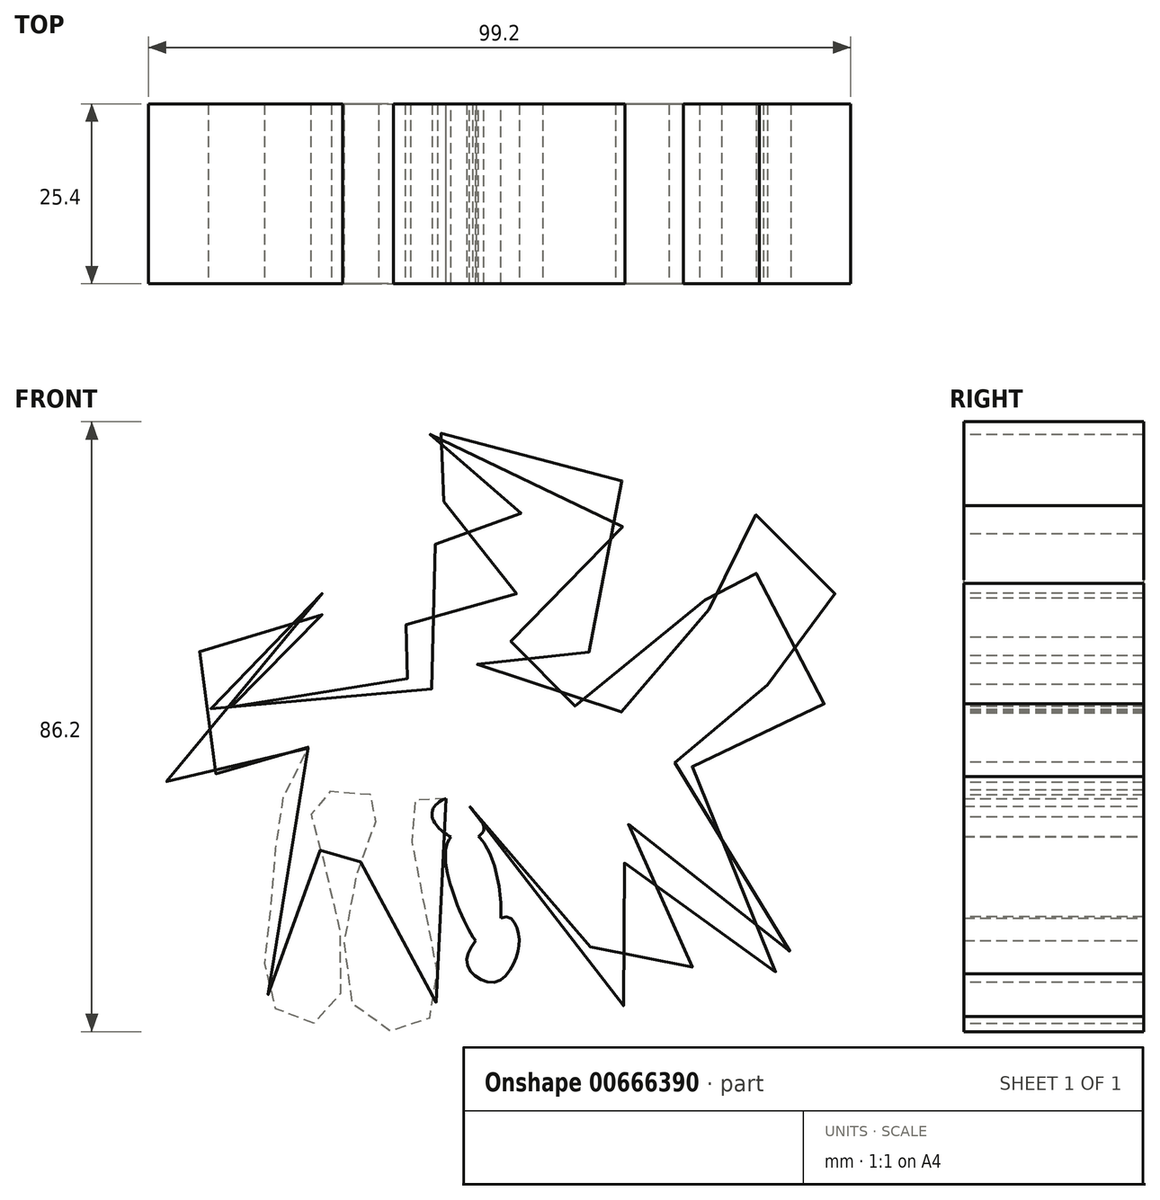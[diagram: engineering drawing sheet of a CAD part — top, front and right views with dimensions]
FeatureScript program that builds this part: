
annotation { "Feature Type Name" : "Feature", "Feature Type Description" : "" }
export const myFeature = defineFeature(function(context is Context, id is Id, definition is map)
    precondition{}
    {
        {
            var Q0;
            Q0=qCreatedBy(makeId("Front.planeOp"),FACE);
            var sketch = newSketch(context, id + "F0", { "sketchPlane" : qUnion([Q0])});
            skFitSpline(sketch, "E0", {"points": [v(-24.68, 12.83) * mm, v(-33.88, 23.4) * mm, v(-26.05, 37.12) * mm, v(-17.24, 28.1) * mm, v(-16.26, 38.88) * mm, v(-34.86, 43.38) * mm, v(-34.47, 50.63) * mm, v(-31.53, 51.22) * mm, v(-7.05, 52) * mm, v(-3.53, 39.27) * mm, v(-4.7, 23.01) * mm, v(-14.1, 20.27) * mm, v(-22.52, 22.43) * mm, v(-24.1, 18.9) * mm, v(-19.78, 15.38) * mm, v(-7.44, 12.44) * mm, v(8.81, 14.2) * mm, v(8.62, 26.74) * mm, v(5.68, 37.7) * mm, v(15.08, 40.25) * mm, v(15.86, 29.09) * mm, v(25.46, 29.67) * mm, v(26.25, 13.42) * mm, v(16.84, 15.77) * mm, v(15.86, 3.62) * mm, v(3.13, 4.8) * mm, v(19.78, -17.53) * mm, v(15.47, -24.78) * mm, v(-3.92, -2.84) * mm, v(0, -16.16) * mm, v(7.25, -27.32) * mm, v(-2.35, -30.26) * mm, v(-14.1, -5.39) * mm, v(-23.7, -1.66) * mm, v(-32.32, 0) * mm, v(-31.93, -13.61) * mm, v(-31.14, -31.63) * mm, v(-40.74, -30.65) * mm, v(-40.15, -8.13) * mm, v(-38.58, 0) * mm, v(-46.62, 0) * mm, v(-45.44, -10.09) * mm, v(-44.85, -30.85) * mm, v(-52.69, -29.67) * mm, v(-52.88, -13.22) * mm, v(-50.34, 2.84) * mm, v(-44.66, 12.05) * mm, v(-58.37, 4.4) * mm, v(-70.12, 3.82) * mm, v(-58.17, 24.97) * mm, v(-43.09, 28.1) * mm, v(-53.86, 21.25) * mm, v(-61.9, 12.63) * mm, v(-50.92, 15.77) * mm, v(-40.54, 18.7) * mm, v(-24.68, 12.83) * mm]});
            skSolve(sketch);
        }
        {
            var Q0;
            Q0=qSketchRegion(id+"F0",true);
            extrude(context, id + "F1", {"entities" : qUnion([Q0]), "depth" : 25.4 * mm});
        }
        {
            var Q0;
            Q0=qCreatedBy(makeId("Front.planeOp"),FACE);
            var sketch = newSketch(context, id + "F2", { "sketchPlane" : qUnion([Q0])});
            skCircle(sketch, "E1", {"center": v(13.71, 35.94) * mm, "radius": 1.58 * mm});
            skSolve(sketch);
        }
        {
            var Q0;
            Q0=qSketchRegion(id+"F2",true);
            extrude(context, id + "F3", {"entities" : qUnion([Q0]), "operationType" : NewBodyOperationType.REMOVE, "oppositeDirection" : true, "depth" : 23.62 * mm});
        }
        {
            var Q0;
            Q0=qCreatedBy(makeId("Front.planeOp"),FACE);
            var sketch = newSketch(context, id + "F4", { "sketchPlane" : qUnion([Q0])});
            skFitSpline(sketch, "E2", {"points": [v(-27.22, 0) * mm, v(-30.36, -1.86) * mm, v(-28.8, -5) * mm, v(-25.07, -5.97) * mm, v(-23.11, -4.6) * mm, v(-24.48, -2.06) * mm, v(-27.22, 0) * mm]});
            skSolve(sketch);
        }
        {
            var Q0;
            Q0=qSketchRegion(id+"F4",true);
            extrude(context, id + "F5", {"entities" : qUnion([Q0]), "operationType" : NewBodyOperationType.ADD, "depth" : 25.4 * mm});
        }
        {
            var Q0;
            Q0=qCreatedBy(makeId("Front.planeOp"),FACE);
            var sketch = newSketch(context, id + "F6", { "sketchPlane" : qUnion([Q0])});
            skFitSpline(sketch, "E3", {"points": [v(-28, -5.97) * mm, v(-26.64, -15.77) * mm, v(-22.72, -21.45) * mm, v(-20.76, -17.73) * mm, v(-24.1, -5.39) * mm, v(-28, -5.97) * mm]});
            skSolve(sketch);
        }
        {
            var Q0;
            Q0=qSketchRegion(id+"F6",true);
            extrude(context, id + "F7", {"entities" : qUnion([Q0]), "operationType" : NewBodyOperationType.ADD, "depth" : 25.4 * mm});
        }
        {
            var Q0;
            Q0=qCreatedBy(makeId("Front.planeOp"),FACE);
            var sketch = newSketch(context, id + "F8", { "sketchPlane" : qUnion([Q0])});
            skFitSpline(sketch, "E4", {"points": [v(-24.29, -20.27) * mm, v(-25.27, -24.19) * mm, v(-21.54, -26.15) * mm, v(-18.6, -22.82) * mm, v(-18.22, -19.3) * mm, v(-19.78, -16.94) * mm, v(-24.29, -20.27) * mm]});
            skSolve(sketch);
        }
        {
            var Q0;
            Q0=qSketchRegion(id+"F8",true);
            extrude(context, id + "F9", {"entities" : qUnion([Q0]), "operationType" : NewBodyOperationType.ADD, "depth" : 25.4 * mm});
        }
        {
            var Q0;
            Q0=qCreatedBy(makeId("Front.planeOp"),FACE);
            var sketch = newSketch(context, id + "F10", { "sketchPlane" : qUnion([Q0])});
            skLineSegment(sketch, "E5", {"start": v(-128.59, 0) * mm, "end": v(90.64, 0) * mm});
            skSolve(sketch);
        }
    });
